# Revit family: Window-Awning-Pella-Architect-Contemporary-Fixed-1
name_source: partatom
category: Windows
revit_build: Autodesk Revit Architecture 2013 (Build: 20130531_2115(x64)
units: mm (PartAtom-declared; Revit-internal decimal feet)

## types (3) — shared parameters
Assembly Code = B2020130
Cladding = Aluminum
Default Sill Height = 3' - 0"
Depth = 0' - 5"
Description = Aluminum Clad Wood Window
Energy Star = http://www.pella.com
Finish = Aluminum-Pella-EnduraClad-White
Glass Thickness = 0' - 0 11/16"
Glazing = Glass-Pella-Low_E-Argon
Grille Height = 1' - 7 9/32"
Grille Width = 2' - 7 9/32"
Height = 2' - 0"
Horizontal Grille Offset = 0' - 6 7/16"
Horizontal Grille Spacing = 0' - 6 7/16"
Horizontal Mullions = 2
Inset = 0' - 0"
Interior Finish = Wood-Pella-Pine
Jamb Extensions = Yes
LEED = http://professional.pella.com
Manufacturer = Pella
Material = Wood - Pine
Max Height = 2' - 5"
Max Lites = 10
Max Width = 4' - 11"
Min Height = 1' - 5"
Min Width = 1' - 5"
Model = Awning Fixed
Mullions = 0' - 0 7/8"
Nail Fin = Yes
Offset = 0' - 0"
Operation = Fixed
Prairie Offset = 0' - 3"
Product Documentation Link = http://media.pella.com
Product Name = Architect Series Contemporary
Product Page URL = http://professional.pella.com
Requested Height = 2' - 0"
Requested Width = 3' - 0"
Rough Height = 2' - 0 3/4"
Rough Width = 3' - 0 3/4"
Specification = http://media.pella.com
Traditional Grille Array Horizontal = No
Traditional Grille Array Vertical = No
Traditional Lites High = 2
Traditional Lites Wide = 2
Type Comments = Awning
URL = http://professional.pella.com
Vertical Grille Offset = 0' - 10 7/16"
Vertical Grille Spacing = 0' - 10 7/16"
Vertical Mullions = 2
Wall Closure = By host
Warranty = https://content.pella.com
Width = 3' - 0"

## per-type parameters (varying)
| type | Analytic Construction | Heat Transfer Coefficient (U) | Prairie Grille | Solar Heat Gain Coefficient | Thermal Resistance (R) | Traditional Grille | Traditional Grille Single Horizontal | Traditional Grille Single Vertical | Visual Light Transmittance |
| Awning Traditional Grille | Double glazing - 1/8 in thick - low-E/clear (e = 0.2) glass | 0.35 BTU/(h·ft²·°F) | No | 0.65 | 2.8573 (h·ft²·°F)/BTU | Yes | Yes | Yes | 0.76 |
| Awning Prairie Grille | Double glazing - 1/8 in thick - low-E/clear (e = 0.2) glass | 0.35 BTU/(h·ft²·°F) | Yes | 0.65 | 2.8573 (h·ft²·°F)/BTU | No | No | No | 0.76 |
| Awning No Grille | <None> | 0.1 BTU/(h·ft²·°F) | No | 0 | 10.0000 (h·ft²·°F)/BTU | No | No | No | 0 |

## geometry (parser evidence)
native form markers: Blend x29, Sweep x7
no freeform markers — native parametric forms only
